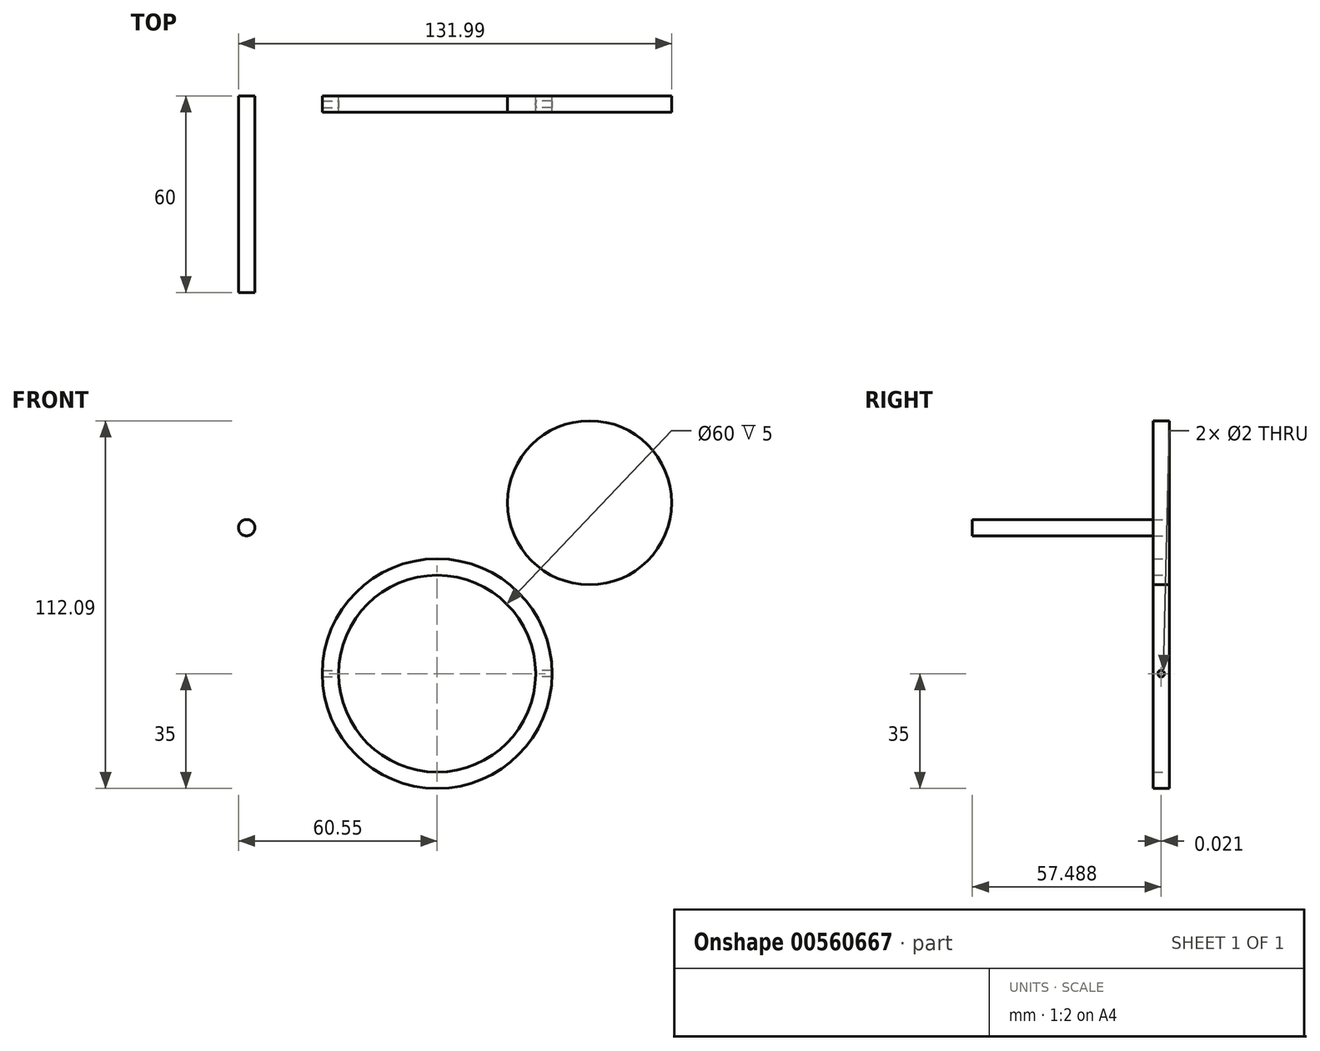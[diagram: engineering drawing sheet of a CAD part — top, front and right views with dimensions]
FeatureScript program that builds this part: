
annotation { "Feature Type Name" : "Feature", "Feature Type Description" : "" }
export const myFeature = defineFeature(function(context is Context, id is Id, definition is map)
    precondition{}
    {
        {
            var Q0;
            Q0=qCreatedBy(makeId("Front.planeOp"),FACE);
            var sketch = newSketch(context, id + "F0", { "sketchPlane" : qUnion([Q0])});
            skCircle(sketch, "E0", {"center": v(0, 0) * mm, "radius": 35 * mm});
            skCircle(sketch, "E1", {"center": v(0, 0) * mm, "radius": 30 * mm});
            skSolve(sketch);
        }
        {
            var Q0;
            Q0=makeQuery(id+"F0.imprint","IMPRINT",FACE,{"disambiguationData":[TD([[makeQuery(id+"F0.imprint","IMPRINT",EDGE,{"derivedFrom":sQuery(id+"F0.wireOp",EDGE,"E0")}),1.0]])]});
            extrude(context, id + "F1", {"entities" : qUnion([Q0]), "depth" : 5 * mm, "offsetDistance" : 25.4 * mm});
        }
        {
            var Q0;
            Q0=qCreatedBy(makeId("Right.planeOp"),FACE);
            var sketch = newSketch(context, id + "F2", { "sketchPlane" : qUnion([Q0])});
            skPoint(sketch, "E2", {"position": v(0, 0) * mm});
            skPoint(sketch, "E3", {"position": v(-2.5, 0) * mm});
            skCircle(sketch, "E4", {"center": v(-2.5, 0) * mm, "radius": 1.5 * mm});
            skLineSegment(sketch, "E5", {"start": v(0, 0) * mm, "end": v(-4.98, 0) * mm});
            skSolve(sketch);
        }
        {
            var Q0;
            Q0=sQuery(id+"F2.wireOp",VERTEX,"E3");
            var Q1;
            Q1=makeQuery(id+"F1.opExtrude","SWEPT_BODY",BODY,{"disambiguationData":[OSD([sQuery(id+"F0.wireOp",EDGE,"E0"),sQuery(id+"F0.wireOp",EDGE,"E1")])]});
            hole(context, id + "F3", {"style" : HoleStyle.SIMPLE, "endStyle" : HoleEndStyle.BLIND, "holeDiameter" : 2 * mm, "holeDepth" : 45 * mm, "isTappedThrough" : true, "tappedDepth" : 12 * mm, "tapClearance" : 3, "startFromSketch" : true, "locations" : qUnion([Q0]), "scope" : qUnion([Q1])});
        }
        {
            var Q0;
            Q0=qCreatedBy(makeId("Right.planeOp"),FACE);
            var sketch = newSketch(context, id + "F4", { "sketchPlane" : qUnion([Q0])});
            skPoint(sketch, "E6", {"position": v(-2.51, 0) * mm});
            skCircle(sketch, "E7", {"center": v(-2.51, 0) * mm, "radius": 1.5 * mm});
            skLineSegment(sketch, "E8", {"start": v(-5.02, 0) * mm, "end": v(0, 0) * mm});
            skSolve(sketch);
        }
        {
            var Q0;
            Q0=sQuery(id+"F4.wireOp",VERTEX,"E6");
            var Q1;
            Q1=makeQuery(id+"F1.opExtrude","SWEPT_BODY",BODY,{"disambiguationData":[OSD([sQuery(id+"F0.wireOp",EDGE,"E0"),sQuery(id+"F0.wireOp",EDGE,"E1")])]});
            hole(context, id + "F5", {"style" : HoleStyle.SIMPLE, "endStyle" : HoleEndStyle.BLIND, "oppositeDirection" : true, "holeDiameter" : 2 * mm, "holeDepth" : 100 * mm, "isTappedThrough" : true, "tappedDepth" : 12 * mm, "tapClearance" : 3, "startFromSketch" : true, "locations" : qUnion([Q0]), "scope" : qUnion([Q1])});
        }
        {
            var Q0;
            Q0=qCreatedBy(makeId("Front.planeOp"),FACE);
            var sketch = newSketch(context, id + "F6", { "sketchPlane" : qUnion([Q0])});
            skCircle(sketch, "E9", {"center": v(46.44, 52.09) * mm, "radius": 25 * mm});
            skSolve(sketch);
        }
        {
            var Q0;
            Q0=makeQuery(id+"F6.imprint","IMPRINT",FACE,{"disambiguationData":[TD([[makeQuery(id+"F6.imprint","IMPRINT",EDGE,{"derivedFrom":sQuery(id+"F6.wireOp",EDGE,"E9")}),1.0]])]});
            extrude(context, id + "F7", {"entities" : qUnion([Q0]), "depth" : 5 * mm, "offsetDistance" : 25 * mm});
        }
        {
            var Q0;
            Q0=qCreatedBy(makeId("Front.planeOp"),FACE);
            var sketch = newSketch(context, id + "F8", { "sketchPlane" : qUnion([Q0])});
            skCircle(sketch, "E10", {"center": v(-58.05, 44.5) * mm, "radius": 2.5 * mm});
            skSolve(sketch);
        }
        {
            var Q0;
            Q0=makeQuery(id+"F8.imprint","IMPRINT",FACE,{"disambiguationData":[TD([[makeQuery(id+"F8.imprint","IMPRINT",EDGE,{"derivedFrom":sQuery(id+"F8.wireOp",EDGE,"E10")}),1.0]])]});
            extrude(context, id + "F9", {"entities" : qUnion([Q0]), "depth" : 60 * mm, "offsetDistance" : 25 * mm});
        }
    });
